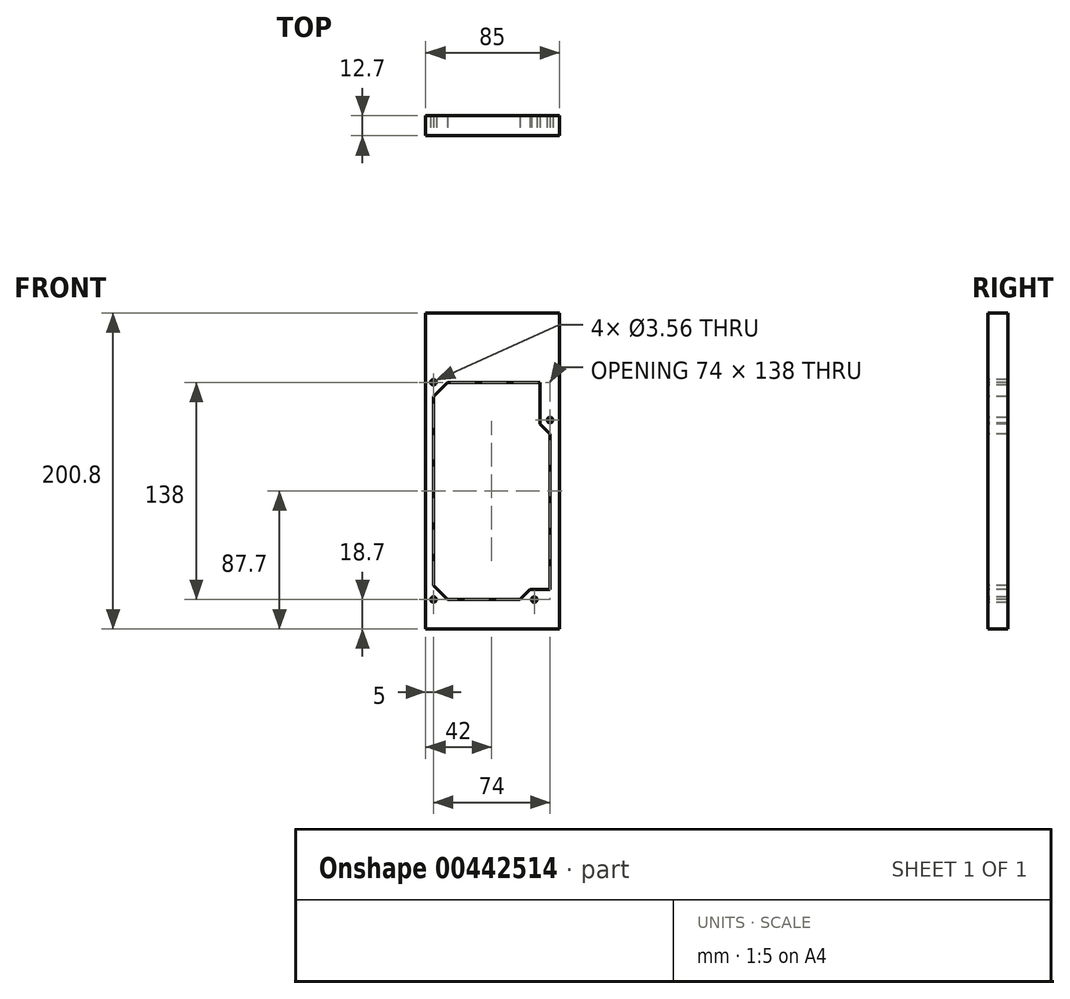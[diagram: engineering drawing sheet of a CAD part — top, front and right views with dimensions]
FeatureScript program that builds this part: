
annotation { "Feature Type Name" : "Feature", "Feature Type Description" : "" }
export const myFeature = defineFeature(function(context is Context, id is Id, definition is map)
    precondition{}
    {
        {
            var Q0;
            Q0=qCreatedBy(makeId("Front.planeOp"),FACE);
            var sketch = newSketch(context, id + "F0", { "sketchPlane" : qUnion([Q0])});
            skLineSegment(sketch, "E0.bottom", {"start": v(42.5, 100.4) * mm, "end": v(-42.5, 100.4) * mm});
            skLineSegment(sketch, "E0.top", {"start": v(42.5, -100.4) * mm, "end": v(-42.5, -100.4) * mm});
            skLineSegment(sketch, "E0.left", {"start": v(42.5, 100.4) * mm, "end": v(42.5, -100.4) * mm});
            skLineSegment(sketch, "E0.right", {"start": v(-42.5, 100.4) * mm, "end": v(-42.5, -100.4) * mm});
            skLineSegment(sketch, "E1", {"start": v(42.5, 100.4) * mm, "end": v(-42.5, -100.4) * mm, "construction": true});
            skSolve(sketch);
        }
        {
            var Q0;
            Q0=makeQuery(id+"F0.imprint","IMPRINT",FACE,{"disambiguationData":[TD([[makeQuery(id+"F0.imprint","IMPRINT",EDGE,{"derivedFrom":sQuery(id+"F0.wireOp",EDGE,"E0.bottom")}),1.0]])]});
            extrude(context, id + "F1", {"entities" : qUnion([Q0]), "depth" : 12.7 * mm});
        }
        {
            var Q0;
            Q0=makeQuery(id+"F1.opExtrude","CAP_FACE",FACE,{"disambiguationData":[OSD([sQuery(id+"F0.wireOp",EDGE,"E0.bottom"),sQuery(id+"F0.wireOp",EDGE,"E0.top"),sQuery(id+"F0.wireOp",EDGE,"E0.left"),sQuery(id+"F0.wireOp",EDGE,"E0.right")])],"isStart":false});
            var sketch = newSketch(context, id + "F2", { "sketchPlane" : qUnion([Q0])});
            skLineSegment(sketch, "E2", {"start": v(-42.5, 87.7) * mm, "end": v(42.5, 87.7) * mm, "construction": true});
            skLineSegment(sketch, "E3", {"start": v(-42.5, -87.7) * mm, "end": v(42.5, -87.7) * mm, "construction": true});
            skSolve(sketch);
        }
        {
            var Q0;
            Q0=makeQuery(id+"F2.imprint","IMPRINT",FACE,{"disambiguationData":[TD([[makeQuery(id+"F2.imprint","IMPRINT",EDGE,{"derivedFrom":makeQuery(id+"F1.opExtrude","CAP_EDGE",EDGE,{"disambiguationData":[OSD([sQuery(id+"F0.wireOp",EDGE,"E0.bottom")])],"isStart":false})}),1.0]])]});
            var sketch = newSketch(context, id + "F3", { "sketchPlane" : qUnion([Q0])});
            skPoint(sketch, "E4", {"position": v(26.5, -81.7) * mm});
            skPoint(sketch, "E5", {"position": v(-37.5, -81.7) * mm});
            skPoint(sketch, "E6", {"position": v(-37.5, 56.3) * mm});
            skPoint(sketch, "E7", {"position": v(36.5, 32.3) * mm});
            skLineSegment(sketch, "E8", {"start": v(-37.5, -81.7) * mm, "end": v(26.5, -81.7) * mm, "construction": true});
            skCircle(sketch, "E9", {"center": v(-37.5, 56.3) * mm, "radius": 1.78 * mm});
            skCircle(sketch, "E10", {"center": v(36.5, 32.3) * mm, "radius": 1.78 * mm});
            skCircle(sketch, "E11", {"center": v(26.5, -81.7) * mm, "radius": 1.78 * mm});
            skCircle(sketch, "E12", {"center": v(-37.5, -81.7) * mm, "radius": 1.78 * mm});
            skSolve(sketch);
        }
        {
            var Q0;
            Q0=qSketchRegion(id+"F3",true);
            extrude(context, id + "F4", {"entities" : qUnion([Q0]), "operationType" : NewBodyOperationType.REMOVE, "endBound" : BoundingType.THROUGH_ALL, "oppositeDirection" : true, "depth" : 25.4 * mm});
        }
        {
            var Q0;
            Q0=makeQuery(id+"F2.imprint","IMPRINT",FACE,{"disambiguationData":[TD([[makeQuery(id+"F2.imprint","IMPRINT",EDGE,{"derivedFrom":makeQuery(id+"F1.opExtrude","CAP_EDGE",EDGE,{"disambiguationData":[OSD([sQuery(id+"F0.wireOp",EDGE,"E0.bottom")])],"isStart":false})}),1.0]])]});
            var sketch = newSketch(context, id + "F5", { "sketchPlane" : qUnion([Q0])});
            skLineSegment(sketch, "E13", {"start": v(-37.5, 47.32) * mm, "end": v(-28.52, 56.3) * mm});
            skLineSegment(sketch, "E14", {"start": v(-28.52, 56.3) * mm, "end": v(30.15, 56.3) * mm});
            skLineSegment(sketch, "E15", {"start": v(30.15, 56.3) * mm, "end": v(30.15, 29.67) * mm});
            skLineSegment(sketch, "E16", {"start": v(30.15, 29.67) * mm, "end": v(36.5, 23.32) * mm});
            skLineSegment(sketch, "E17", {"start": v(36.5, 23.32) * mm, "end": v(36.5, -75.35) * mm});
            skLineSegment(sketch, "E18", {"start": v(17.52, -81.7) * mm, "end": v(-28.52, -81.7) * mm});
            skLineSegment(sketch, "E19", {"start": v(-28.52, -81.7) * mm, "end": v(-37.5, -72.72) * mm});
            skLineSegment(sketch, "E20", {"start": v(-37.5, -72.72) * mm, "end": v(-37.5, 47.32) * mm});
            skCircle(sketch, "E21.0", {"center": v(-37.5, 56.3) * mm, "radius": 1.78 * mm, "construction": true});
            skCircle(sketch, "E22.0", {"center": v(36.5, 32.3) * mm, "radius": 1.78 * mm});
            skCircle(sketch, "E23.0", {"center": v(-37.5, -81.7) * mm, "radius": 1.78 * mm});
            skLineSegment(sketch, "E24", {"start": v(17.52, -81.7) * mm, "end": v(23.87, -75.35) * mm});
            skLineSegment(sketch, "E25", {"start": v(23.87, -75.35) * mm, "end": v(36.5, -75.35) * mm});
            skCircle(sketch, "E26.0", {"center": v(26.5, -81.7) * mm, "radius": 1.78 * mm});
            skSolve(sketch);
        }
        {
            var Q0;
            Q0=qSketchRegion(id+"F5",true);
            extrude(context, id + "F6", {"entities" : qUnion([Q0]), "operationType" : NewBodyOperationType.REMOVE, "endBound" : BoundingType.THROUGH_ALL, "oppositeDirection" : true, "depth" : 25.4 * mm});
        }
    });
